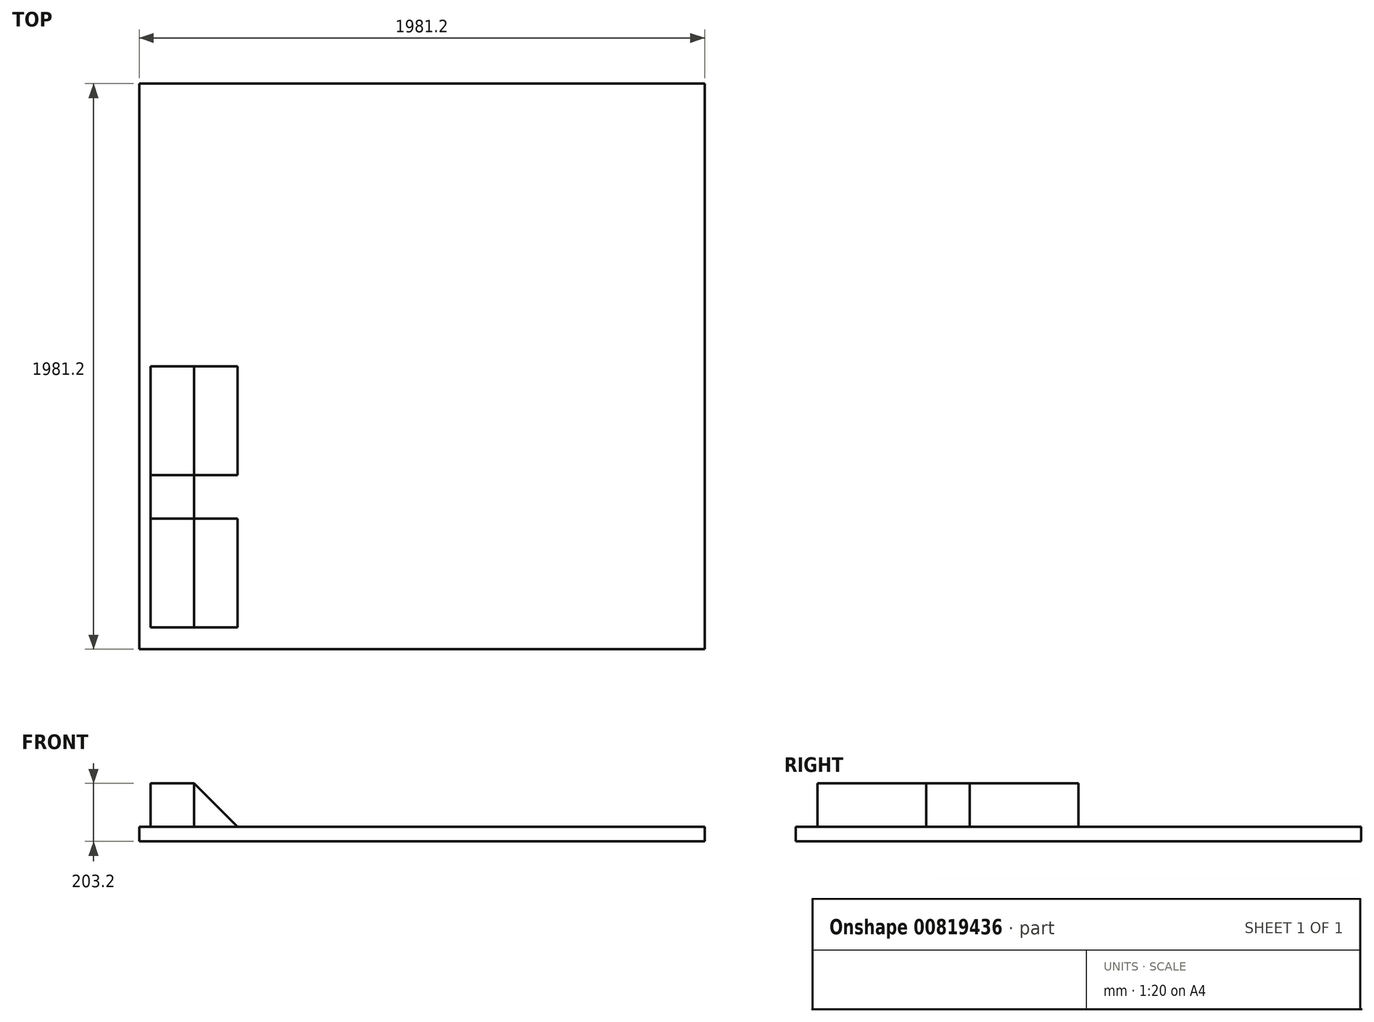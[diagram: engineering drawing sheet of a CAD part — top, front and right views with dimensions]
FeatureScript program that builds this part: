
annotation { "Feature Type Name" : "Feature", "Feature Type Description" : "" }
export const myFeature = defineFeature(function(context is Context, id is Id, definition is map)
    precondition{}
    {
        {
            var Q0;
            Q0=qCreatedBy(makeId("Top.planeOp"),FACE);
            var sketch = newSketch(context, id + "F0", { "sketchPlane" : qUnion([Q0])});
            skLineSegment(sketch, "E0.bottom", {"start": v(-980.35, 1345.32) * mm, "end": v(1000.85, 1345.32) * mm});
            skLineSegment(sketch, "E0.top", {"start": v(-980.35, -635.88) * mm, "end": v(1000.85, -635.88) * mm});
            skLineSegment(sketch, "E0.left", {"start": v(-980.35, 1345.32) * mm, "end": v(-980.35, -635.88) * mm});
            skLineSegment(sketch, "E0.right", {"start": v(1000.85, 1345.32) * mm, "end": v(1000.85, -635.88) * mm});
            skSolve(sketch);
        }
        {
            var Q0;
            Q0=makeQuery(id+"F0.imprint","IMPRINT",FACE,{"disambiguationData":[TD([[makeQuery(id+"F0.imprint","IMPRINT",EDGE,{"derivedFrom":sQuery(id+"F0.wireOp",EDGE,"E0.bottom")}),-1.0]])]});
            extrude(context, id + "F1", {"entities" : qUnion([Q0]), "oppositeDirection" : true, "depth" : 50.8 * mm, "offsetDistance" : 25.4 * mm});
        }
        {
            var Q0;
            Q0=makeQuery(id+"F1.opExtrude","SWEPT_FACE",FACE,{"disambiguationData":[OSD([sQuery(id+"F0.wireOp",EDGE,"E0.top")])]});
            cPlane(context, id + "F2", {"entities" : qUnion([Q0]), "cplaneType" : CPlaneType.OFFSET, "offset" : 76.2 * mm, "oppositeDirection" : true, "width" : 152.4 * mm, "height" : 152.4 * mm});
        }
        {
            var Q0;
            Q0=qCreatedBy(id+"F2.planeOp",FACE);
            var sketch = newSketch(context, id + "F3", { "sketchPlane" : qUnion([Q0])});
            skLineSegment(sketch, "E1", {"start": v(-787.62, 0) * mm, "end": v(-635.22, 0) * mm});
            skLineSegment(sketch, "E2", {"start": v(-787.62, 0) * mm, "end": v(-787.62, 152.4) * mm});
            skLineSegment(sketch, "E3", {"start": v(-787.62, 152.4) * mm, "end": v(-635.22, 0) * mm});
            skSolve(sketch);
        }
        {
            var Q0;
            Q0=makeQuery(id+"F3.imprint","IMPRINT",FACE,{"disambiguationData":[TD([[makeQuery(id+"F3.imprint","IMPRINT",EDGE,{"derivedFrom":sQuery(id+"F3.wireOp",EDGE,"E1")}),1.0]])]});
            extrude(context, id + "F4", {"entities" : qUnion([Q0]), "oppositeDirection" : true, "depth" : 381 * mm, "offsetDistance" : 25.4 * mm});
        }
        {
            var Q0;
            Q0=makeQuery(id+"F4.opExtrude","SWEPT_FACE",FACE,{"disambiguationData":[OSD([sQuery(id+"F3.wireOp",EDGE,"E2")])]});
            extrude(context, id + "F5", {"entities" : qUnion([Q0]), "depth" : 152.4 * mm, "offsetDistance" : 25.4 * mm});
        }
        {
            var Q0;
            {var subQ0=sQuery(id+"F3.wireOp",EDGE,"E2");Q0=makeQuery(id+"F5.boolean.opBoolean","MERGE",FACE,{"derivedFrom":[makeQuery(id+"F4.opExtrude","CAP_FACE",FACE,{"disambiguationData":[OSD([sQuery(id+"F3.wireOp",EDGE,"E1"),subQ0,sQuery(id+"F3.wireOp",EDGE,"E3")])],"isStart":false}),makeQuery(id+"F5.opExtrude","SWEPT_FACE",FACE,{"disambiguationData":[OSD([subQ0]),TDD([makeQuery(id+"F4.opExtrude","CAP_EDGE",EDGE,{"disambiguationData":[OSD([subQ0])],"isStart":false})])]})]});}
            var sketch = newSketch(context, id + "F6", { "sketchPlane" : qUnion([Q0])});
            skLineSegment(sketch, "E4.bottom", {"start": v(787.62, 152.4) * mm, "end": v(940.02, 152.4) * mm});
            skLineSegment(sketch, "E4.top", {"start": v(787.62, 0) * mm, "end": v(940.02, 0) * mm});
            skLineSegment(sketch, "E4.left", {"start": v(787.62, 152.4) * mm, "end": v(787.62, 0) * mm});
            skLineSegment(sketch, "E4.right", {"start": v(940.02, 152.4) * mm, "end": v(940.02, 0) * mm});
            skSolve(sketch);
        }
        {
            var Q0;
            Q0 = qSketchRegion(id + "F6", true);
            extrude(context, id + "F7", {"entities" : qUnion([Q0]), "depth" : 152.4 * mm, "offsetDistance" : 25.4 * mm});
        }
        {
            var Q0;
            Q0=makeQuery(id+"F4.opExtrude","SWEPT_BODY",BODY,{"disambiguationData":[OSD([sQuery(id+"F3.wireOp",EDGE,"E1"),sQuery(id+"F3.wireOp",EDGE,"E2"),sQuery(id+"F3.wireOp",EDGE,"E3")])]});
            transform(context, id + "F8", {"entities" : qUnion([Q0]), "transformType" : TransformType.TRANSLATION_3D, "dx" : 0 * mm, "dy" : 533.4 * mm, "dz" : 0 * mm, "makeCopy" : true});
        }
        {
            var Q0;
            Q0=makeQuery(id+"F5.opExtrude","SWEPT_BODY",BODY,{"disambiguationData":[OSD([sQuery(id+"F3.wireOp",EDGE,"E2")])]});
            transform(context, id + "F9", {"entities" : qUnion([Q0]), "transformType" : TransformType.TRANSLATION_3D, "dx" : 0 * mm, "dy" : 533.4 * mm, "dz" : 0 * mm, "makeCopy" : true});
        }
    });
